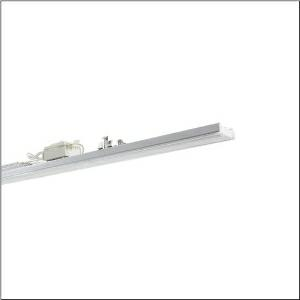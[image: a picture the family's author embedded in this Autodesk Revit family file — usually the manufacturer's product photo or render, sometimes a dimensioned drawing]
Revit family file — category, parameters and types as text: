
# Revit family: licross_r__21_recessed_ho_52tl18de47xm_4b87
name_source: partatom
category: Lighting Fixtures
units: mm (PartAtom-declared; Revit-internal decimal feet)

## family parameters
Cut with Voids When Loaded = No
Host = Face
Light Source = No
Part Type = Normal
Room Calculation Point = No
Round Connector Dimension = Use Diameter
Shared = No

## types (1)
- --- (1 x LED, 7420 lm, 44.1 W, 4000K)
    Apparent Load = 44 VA
    CIE Flux Codes = 75 94 99 100 100
    Color Rendering = 80
    Color Temperature = 4000K
    Default Elevation = 1800 mm
    Description = Licross® 21 Recessed HO, luminaire insert, of sheet steel, galvanised, coil coated, white, length: 750mm, width: 66mm, height: 67mm, LED rated luminous flux: 7.420lm, light colour: 840, control gear: DALI 2, with plug, 5-pole, with phase selection, mains connection: 220..240V, AC, 50/60Hz, rated input power: 44W, internal wiring halogen-free, primary light control with lens, of plastic, primary optical cover: cover, of PMMA, light emission: direct distribution, primary light characteristic: symmetric, protection rating (complete): IP40, insulation class (complete): insulation class I (protective earthing), certification: CE, ENEC, VDE, UKCA, protection symbol: D if used in an environment without relevant dust loads with corresponding accessories, impact resistance: IK06, permissible ambient temperature for indoor applications: -25..+30°C, corresponds to IFS (International Featured Standards) requirements for safety and quality in the food industry, reducing of maximum allowable ambient temperature of 5°C with ceiling mounting, LABS conformity tested according to VDMA 24364:2018-05, packaging unit: 1 piece
    Height = 58 mm
    Lamp = 1 x LED
    Lamp Light Flux = 7420 lm
    Lamp Power = 44.1 W
    Lamp count = 1
    Length = 750 mm
    Luminous efficacy = 168 lm/W
    Manufacturer = Siteco
    ModVariant = No
    Model = 52TL18DE47XM
    Mounting Place = Ceiling
    Mounting Type = Pendant
    Number of Poles = 1
    OnlyDefault = Yes
    Power Factor = 1
    Product Name = Licross® 21 Recessed HO
    Product group = luminaire insert | ceiling pendant
    ProductGroupID = 902
    Protection Class = Protection class I
    Protection Degree = IP 40
    RLX_Detail_Level = 1
    RLX_Emergency_Light_Flux = 0 lm
    RLX_Emergency_Type = 0
    RLX_Emergency_Type_DB = No
    RlxData = <blob elided: 29185 chars, md5=99bcdedb>
    Socket = socket
    Standby Power = 0 W
    System Light Flux = 7420 lm
    System Power = 44 W
    Type Comments = factory setting: luminous flux: 100 % | dim-lin: 254 | 484 mA
    Type Image = l_1296930.jpg
    URL = http://relux.com
    VarID = @adj_147399
    Voltage = 0 V
    Weight = 0.00 kg
    Width = 66 mm

## geometry (parser evidence)
native form markers: Blend x4, Sweep x9
no freeform markers — native parametric forms only
